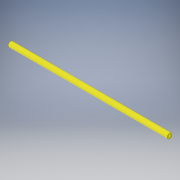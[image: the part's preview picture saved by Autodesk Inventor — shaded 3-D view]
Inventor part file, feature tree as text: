
AUTODESK INVENTOR PART (.ipt)
format: ipt  version: 2017 SP1 (Build 210196100, 196)  size: 92,160 bytes
history: native  units: in
note: dims shown in document units (in); Inventor stores cm internally (conversion verified against a paired STEP export)
features: extrude x1, sketch x1
ambient origin geometry x8: Origin, YZ Plane, XZ Plane, XY Plane, X Axis, Y Axis, Z Axis, Center Point
bodies: Solid1 (feature_tree)
feature tree (2):
  extrude  "Extrusion1"  Depth=0.25in
  sketch  "Sketch1"  dims[d0=0.5in d1=0.25in d2=16.0in d3=0.0in]
